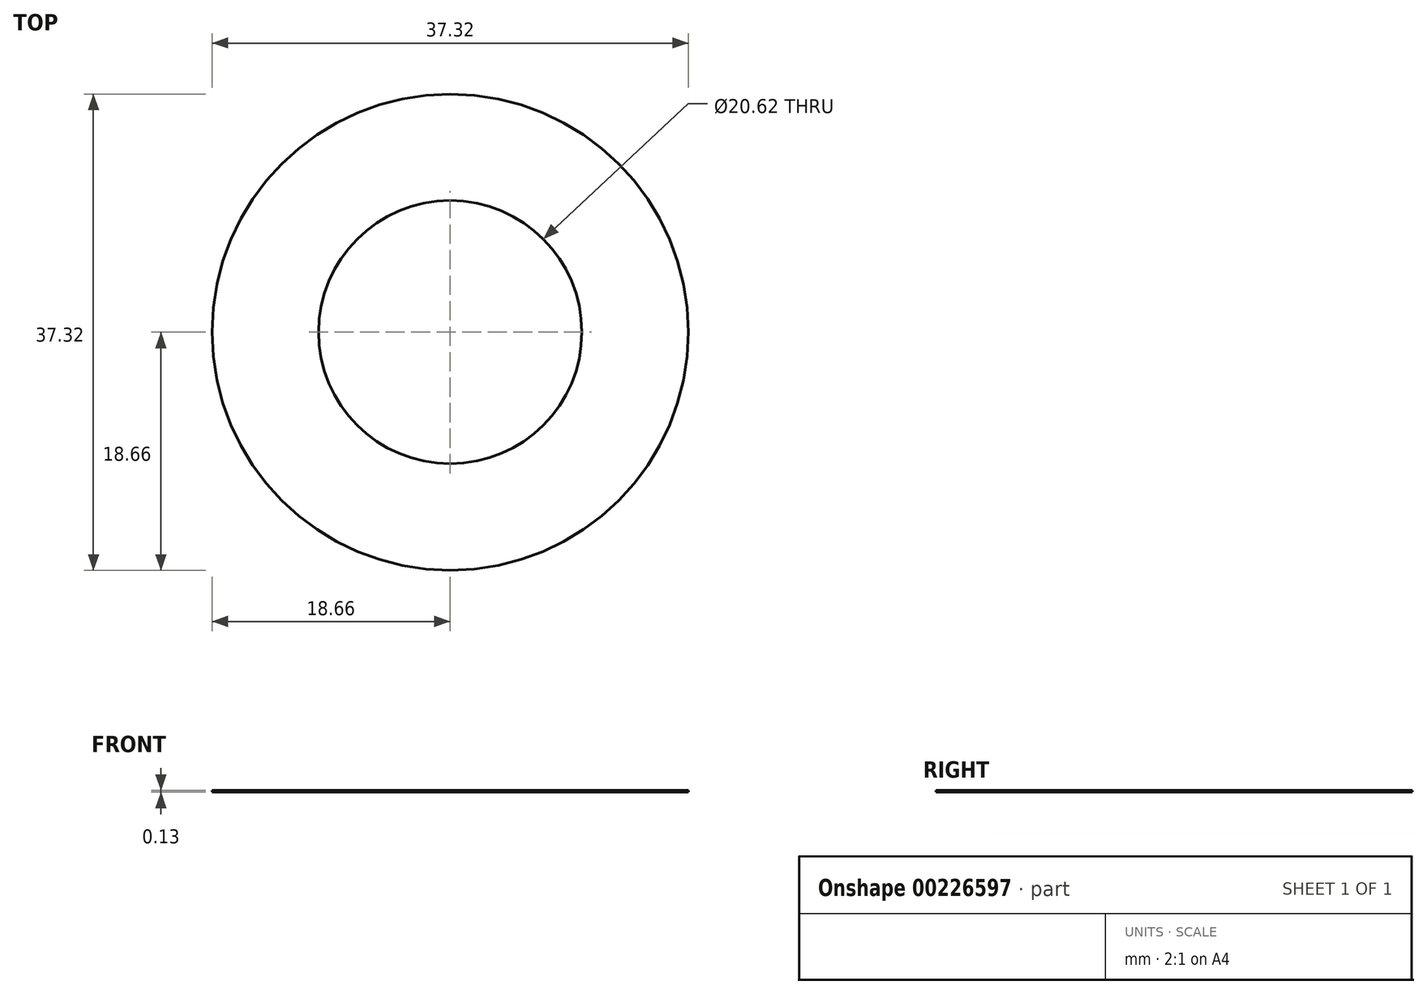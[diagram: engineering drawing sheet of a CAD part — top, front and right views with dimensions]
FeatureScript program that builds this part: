
annotation { "Feature Type Name" : "Feature", "Feature Type Description" : "" }
export const myFeature = defineFeature(function(context is Context, id is Id, definition is map)
    precondition{}
    {
        {
            var Q0;
            Q0=qCreatedBy(makeId("Top.planeOp"),FACE);
            var sketch = newSketch(context, id + "F0", { "sketchPlane" : qUnion([Q0])});
            skCircle(sketch, "E0", {"center": v(0, 0) * mm, "radius": 10.31 * mm});
            skCircle(sketch, "E1", {"center": v(0, 0) * mm, "radius": 18.66 * mm});
            skSolve(sketch);
        }
        {
            var Q0;
            Q0=makeQuery(id+"F0.imprint","IMPRINT",FACE,{"disambiguationData":[TD([[makeQuery(id+"F0.imprint","IMPRINT",EDGE,{"derivedFrom":sQuery(id+"F0.wireOp",EDGE,"E0")}),-1.0]])]});
            extrude(context, id + "F1", {"entities" : qUnion([Q0]), "depth" : ((.108 + .16) / 2) * mm});
        }
    });
